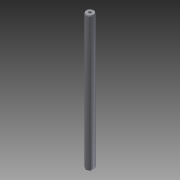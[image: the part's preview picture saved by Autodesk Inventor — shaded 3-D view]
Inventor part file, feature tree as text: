
AUTODESK INVENTOR PART (.ipt)
format: ipt  version: 2016 (Build 200138000, 138)  size: 144,384 bytes
history: native  units: mm
features: other x11, sketch x3, chamfer x2, hole x2, extrude x1
ambient origin geometry x8: Origin, YZ Plane, XZ Plane, XY Plane, X Axis, Y Axis, Z Axis, Center Point
bodies: Solid1 (feature_tree)
feature tree (19):
  other  "Table"
  other  "ER025_CageRod"
  other  "ER05_CageRod"
  other  "ER1_CageRod"
  other  "ER1.5_CageRod"
  other  "ER2_CageRod"
  other  "ER3_CageRod"
  other  "ER4_CageRod"
  other  "ER6_CageRod"
  other  "ER8_CageRod"
  other  "ER10_CageRod"
  extrude  "Extrusion1"  TaperAngle=0.0deg  [1 undecoded]
  chamfer  "Chamfer1"  Distance=0.254mm Angle=45.0deg
  chamfer  "Chamfer2"  Distance=0.254mm Angle=45.0deg
  sketch  "Sketch2"  dims[d9=2.156mm d10=6.0mm d11=4.0mm d12=2.0mm d13=90.0deg d14=5.0mm d15=20.594885mm]
  sketch  "Sketch3"  dims[d16=2.156mm d17=6.0mm d18=4.0mm d19=2.0mm d20=90.0deg d21=5.0mm d22=20.594885mm]
  hole  "Hole1"  [1 undecoded]
  hole  "Hole2"  [1 undecoded]
  sketch  "Sketch1"  dims[d0=6.0mm d2=0.0mm d3=0.254mm d4=0.762mm d5=45.0deg d6=0.254mm d7=0.762mm d8=45.0deg]
note: 3 required parameter values undecoded (feature->parameter linkage not recoverable at this tier; creation-order binding heuristic only, values carry confidence <= 0.55)
